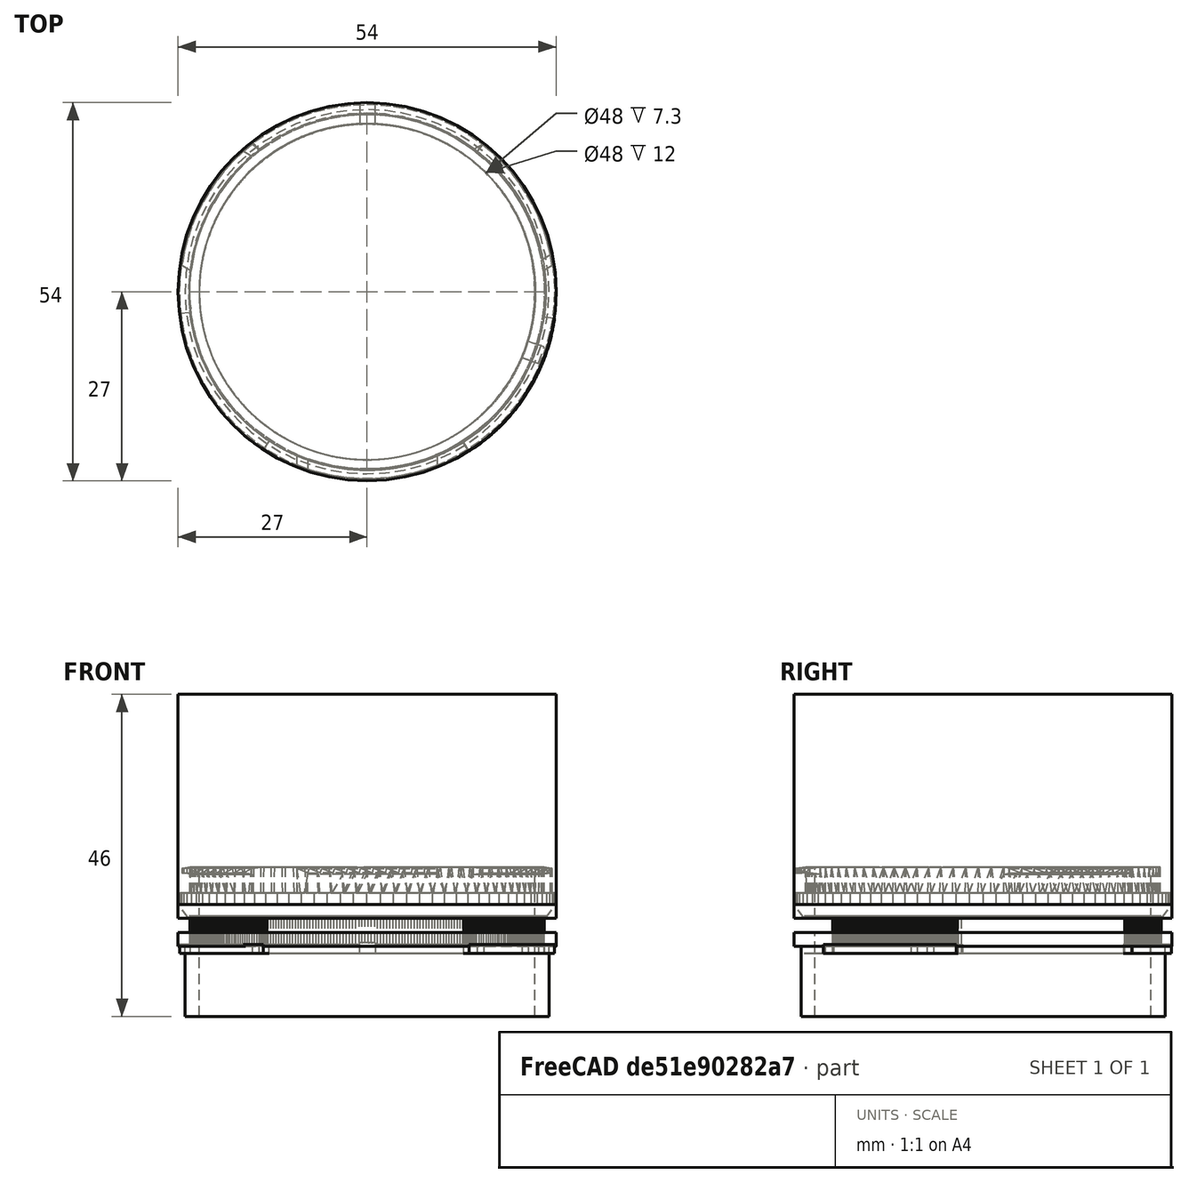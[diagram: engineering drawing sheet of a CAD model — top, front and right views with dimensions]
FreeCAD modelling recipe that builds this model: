
FCSTD DOCUMENT  (FreeCAD 0.16R6712 (Git))
Label: canon_fd_e
License: All rights reserved
LicenseURL: http://en.wikipedia.org/wiki/All_rights_reserved
objects: Part::Cylinder×5, Part::Feature×4, Mesh::Feature×3, Part::Cut×3, Part::Part2DObjectPython×3, Part::MultiFuse×2, Part::Box×1, Part::Cone×1
note: 19 computed .brp shape members not serialized (recipe doc carries the construction recipe); baked Part::Feature solids carry a one-line shape summary decoded from their .brp

FEATURE [Mesh::Feature] Bague_CanonFD
  Placement = pos=(-26.7,-25.7,-1) rot=(0,0,1;0rad)
FEATURE [Part::Cylinder] Cylinder  label="agujero"
  Angle = 360
  Height = 16
  Placement = pos=(0,0,-2) rot=(0,0,1;0rad)
  Radius = 24
FEATURE [Part::Cylinder] Cylinder001  label="anillo"
  Angle = 360
  Height = 10
  Radius = 26
FEATURE [Part::Cylinder] Cylinder002  label="externo"
  Angle = 360
  Height = 2
  Placement = pos=(0,0,10) rot=(0,0,1;0rad)
  Radius = 27
FEATURE [Part::MultiFuse] Fusion
  Shapes = -> [Cylinder001,Cylinder002]
FEATURE [Part::Cut] Cut
  Base = -> Fusion
  Tool = -> Cylinder
FEATURE [Part::Part2DObjectPython] Line  # Draft 2D object (typed FeaturePython)
  ChamferSize = 0
  Closed = false
  End = (0,30,12)
  FilletRadius = 0
  Length = 30
  MakeFace = true
  Points = (2) [(-3.55271e-14,-3.40863e-14,12),(-1.77636e-14,30,12)]
  Start = (0,0,12)
  Subdivisions = 0
FEATURE [Part::Part2DObjectPython] Line001  # Draft 2D object (typed FeaturePython)
  ChamferSize = 0
  Closed = false
  End = (-30,-30,12)
  FilletRadius = 0
  Length = 42.4264
  MakeFace = true
  Points = (2) [(-3.55271e-14,-3.40863e-14,12),(-30,-30,12)]
  Start = (0,0,12)
  Subdivisions = 0
FEATURE [Part::Part2DObjectPython] Line002  # Draft 2D object (typed FeaturePython)
  ChamferSize = 0
  Closed = false
  End = (30,-30,12)
  FilletRadius = 0
  Length = 42.4264
  MakeFace = true
  Points = (2) [(-3.55271e-14,-3.40863e-14,12),(30,-30,12)]
  Start = (0,0,12)
  Subdivisions = 0
FEATURE [Mesh::Feature] Canon_FD_Flange
FEATURE [Part::Feature] Canon_FD_Flange001
  shape: bbox 53.56 x 52.48 x 5.3 mm, 6536 faces, 0 solids (baked)
FEATURE [Part::Feature] Canon_FD_Flange001_solid  label="Canon_FD_Flange001 (Solid)"
  Placement = pos=(0,0.7,9) rot=(0,0,1;0rad)
  shape: bbox 53.56 x 52.48 x 5.3 mm, 6536 faces (baked)
FEATURE [Mesh::Feature] _0mm  label="20mm"
FEATURE [Part::Feature] _0mm001
  shape: bbox 65.5 x 65.47 x 25.3 mm, 3558 faces, 0 solids (baked)
FEATURE [Part::Feature] _0mm001_solid  label="_0mm001 (Solid)"
  shape: bbox 65.5 x 65.47 x 25.3 mm, 3558 faces (baked)
FEATURE [Part::Box] Box  label="Cubo"
  Height = 20
  Length = 80
  Placement = pos=(-37,-40,0) rot=(0,0,1;0rad)
  Width = 80
FEATURE [Part::Cut] Cut001
  Base = -> _0mm001_solid
  Placement = pos=(0,0,-4) rot=(0,0,1;0rad)
  Tool = -> Box
FEATURE [Part::Cylinder] Cylinder003  label="Cilindro"
  Angle = 360
  Height = 55
  Radius = 24
FEATURE [Part::Cylinder] Cylinder004  label="Cilindro001"
  Angle = 360
  Height = 32
  Placement = pos=(0,0,14) rot=(0,0,1;0rad)
  Radius = 27
FEATURE [Part::Cone] Cone  label="Cono"
  Angle = 360
  Height = 2
  Placement = pos=(0,0,14) rot=(0,0,1;0rad)
  Radius1 = 25.5
  Radius2 = 27
FEATURE [Part::MultiFuse] Fusion001
  Shapes = -> [Cut001,Cone]
FEATURE [Part::Cut] Cut002
  Base = -> Fusion001
  Tool = -> Cylinder003
